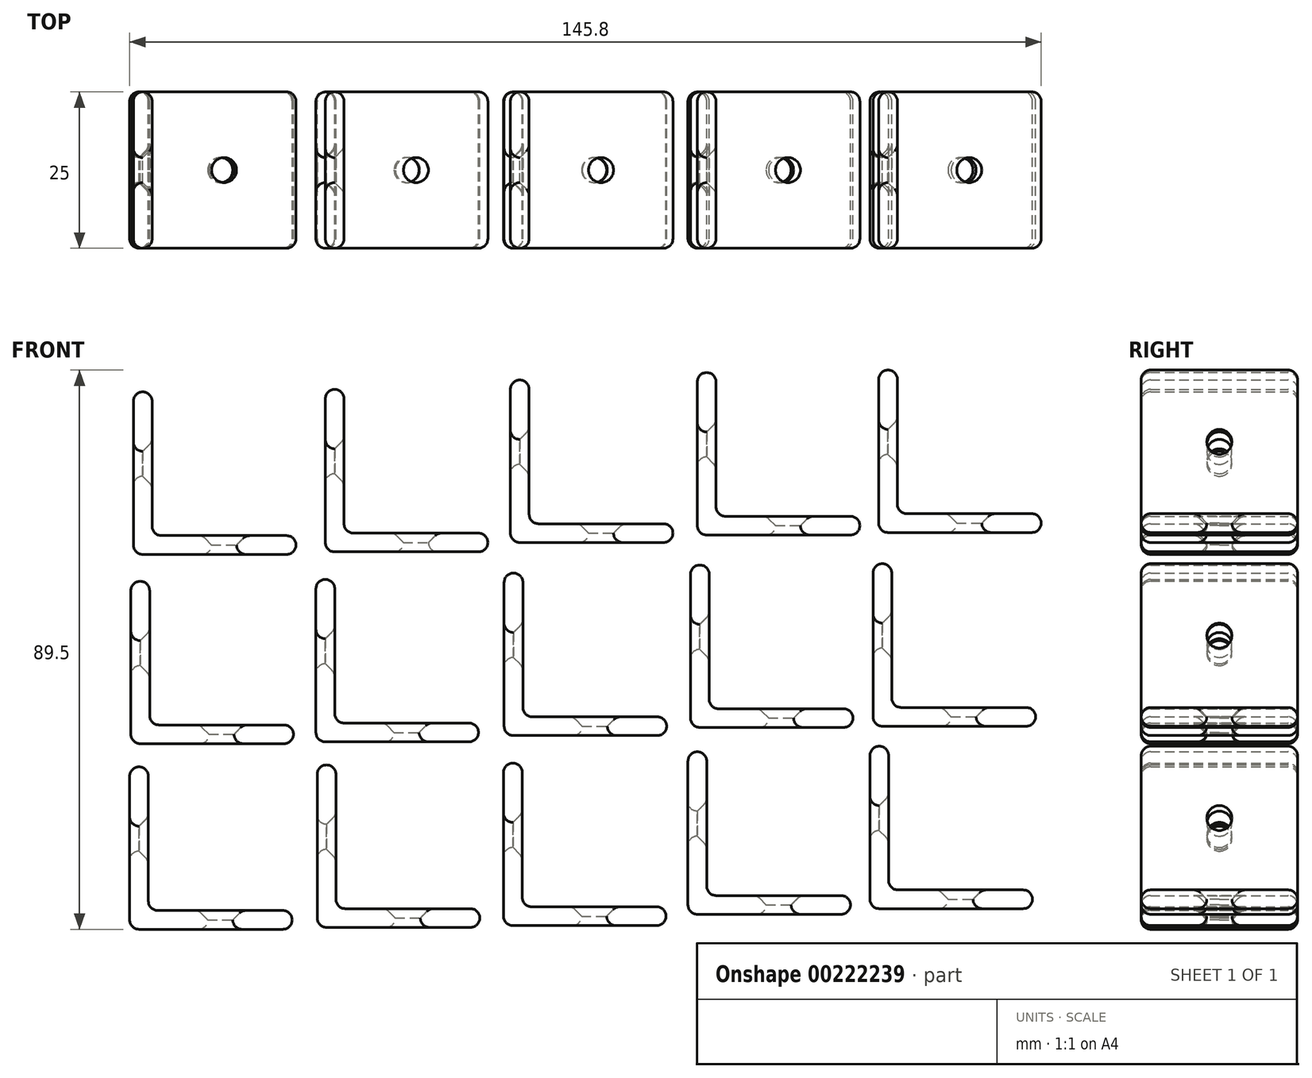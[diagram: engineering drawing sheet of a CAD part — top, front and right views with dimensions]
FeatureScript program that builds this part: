
annotation { "Feature Type Name" : "Feature", "Feature Type Description" : "" }
export const myFeature = defineFeature(function(context is Context, id is Id, definition is map)
    precondition{}
    {
        {
            var Q0;
            Q0=qCreatedBy(makeId("Front.planeOp"),FACE);
            var sketch = newSketch(context, id + "F0", { "sketchPlane" : qUnion([Q0])});
            skLineSegment(sketch, "E0.bottom", {"start": v(13, 13) * mm, "end": v(-13, 13) * mm});
            skLineSegment(sketch, "E0.top", {"start": v(13, -13) * mm, "end": v(-13, -13) * mm});
            skLineSegment(sketch, "E0.left", {"start": v(13, 13) * mm, "end": v(13, -13) * mm});
            skLineSegment(sketch, "E0.right", {"start": v(-13, 13) * mm, "end": v(-13, -13) * mm});
            skPoint(sketch, "E0.middle", {"position": v(0, 0) * mm});
            skLineSegment(sketch, "E1.bottom", {"start": v(13, 13) * mm, "end": v(-10, 13) * mm});
            skLineSegment(sketch, "E1.top", {"start": v(13, -10) * mm, "end": v(-10, -10) * mm});
            skLineSegment(sketch, "E1.left", {"start": v(13, 13) * mm, "end": v(13, -10) * mm});
            skLineSegment(sketch, "E1.right", {"start": v(-10, 13) * mm, "end": v(-10, -10) * mm});
            skSolve(sketch);
        }
        {
            var Q0;
            {var subQ2=sQuery(id+"F0.wireOp",EDGE,"E0.top");Q0=makeQuery(id+"F0.imprint","IMPRINT",FACE,{"disambiguationData":[TD([[makeQuery(id+"F0.imprint","IMPRINT",EDGE,{"derivedFrom":subQ2}),-1.0]])]});}
            extrude(context, id + "F1", {"entities" : qUnion([Q0]), "depth" : 25 * mm, "offsetDistance" : 25 * mm});
        }
        {
            var Q0;
            Q0=makeQuery(id+"F1.opExtrude","SWEPT_FACE",FACE,{"disambiguationData":[OSD([sQuery(id+"F0.wireOp",EDGE,"E1.right")])]});
            var sketch = newSketch(context, id + "F2", { "sketchPlane" : qUnion([Q0])});
            skLineSegment(sketch, "E2", {"start": v(-25, 13) * mm, "end": v(0, -10) * mm, "construction": true});
            skLineSegment(sketch, "E3", {"start": v(0, 13) * mm, "end": v(-25, -10) * mm, "construction": true});
            skPoint(sketch, "E4", {"position": v(-12.5, 1.5) * mm});
            skSolve(sketch);
        }
        {
            var Q0;
            Q0=makeQuery(id+"F1.opExtrude","SWEPT_FACE",FACE,{"disambiguationData":[OSD([sQuery(id+"F0.wireOp",EDGE,"E1.top")])]});
            var sketch = newSketch(context, id + "F3", { "sketchPlane" : qUnion([Q0])});
            skLineSegment(sketch, "E5", {"start": v(-10, -25) * mm, "end": v(13, 0) * mm, "construction": true});
            skLineSegment(sketch, "E6", {"start": v(-10, 0) * mm, "end": v(13, -25) * mm, "construction": true});
            skPoint(sketch, "E7", {"position": v(1.5, -12.5) * mm});
            skSolve(sketch);
        }
        {
            var Q0;
            Q0=sQuery(id+"F3.wireOp",VERTEX,"E7");
            var Q1;
            Q1=sQuery(id+"F2.wireOp",VERTEX,"E4");
            var Q2;
            Q2=makeQuery(id+"F1.opExtrude","SWEPT_BODY",BODY,{"disambiguationData":[OSD([sQuery(id+"F0.wireOp",EDGE,"E0.bottom"),sQuery(id+"F0.wireOp",EDGE,"E0.top"),sQuery(id+"F0.wireOp",EDGE,"E0.left"),sQuery(id+"F0.wireOp",EDGE,"E0.right"),sQuery(id+"F0.wireOp",EDGE,"E1.top"),sQuery(id+"F0.wireOp",EDGE,"E1.right")])]});
            hole(context, id + "F4", {"style" : HoleStyle.C_SINK, "endStyle" : HoleEndStyle.BLIND, "holeDiameter" : 4 * mm, "cSinkDiameter" : 7 * mm, "cSinkAngle" : 90 * degree, "majorDiameter" : 5 * mm, "holeDepth" : 7 * mm, "isTappedThrough" : true, "tappedDepth" : 12 * mm, "tapClearance" : 3, "locations" : qUnion([Q0, Q1]), "scope" : qUnion([Q2])});
        }
        {
            var Q0;
            Q0=makeQuery(id+"F1.opExtrude","SWEPT_FACE",FACE,{"disambiguationData":[OSD([sQuery(id+"F0.wireOp",EDGE,"E0.bottom")])]});
            var Q1;
            Q1=makeQuery(id+"F1.opExtrude","SWEPT_FACE",FACE,{"disambiguationData":[OSD([sQuery(id+"F0.wireOp",EDGE,"E0.right")])]});
            var Q2;
            Q2=makeQuery(id+"F1.opExtrude","SWEPT_FACE",FACE,{"disambiguationData":[OSD([sQuery(id+"F0.wireOp",EDGE,"E0.top")])]});
            var Q3;
            Q3=makeQuery(id+"F1.opExtrude","SWEPT_FACE",FACE,{"disambiguationData":[OSD([sQuery(id+"F0.wireOp",EDGE,"E0.left")])]});
            var Q4;
            Q4=makeQuery(id+"F1.opExtrude","SWEPT_FACE",FACE,{"disambiguationData":[OSD([sQuery(id+"F0.wireOp",EDGE,"E1.right")])]});
            var Q5;
            Q5=makeQuery(id+"F1.opExtrude","SWEPT_FACE",FACE,{"disambiguationData":[OSD([sQuery(id+"F0.wireOp",EDGE,"E1.top")])]});
            var Q6;
            Q6=makeQuery(id+"F1.opExtrude","CAP_FACE",FACE,{"disambiguationData":[OSD([sQuery(id+"F0.wireOp",EDGE,"E0.bottom"),sQuery(id+"F0.wireOp",EDGE,"E0.top"),sQuery(id+"F0.wireOp",EDGE,"E0.left"),sQuery(id+"F0.wireOp",EDGE,"E0.right"),sQuery(id+"F0.wireOp",EDGE,"E1.top"),sQuery(id+"F0.wireOp",EDGE,"E1.right")])],"isStart":true});
            var Q7;
            Q7=makeQuery(id+"F1.opExtrude","CAP_FACE",FACE,{"disambiguationData":[OSD([sQuery(id+"F0.wireOp",EDGE,"E0.bottom"),sQuery(id+"F0.wireOp",EDGE,"E0.top"),sQuery(id+"F0.wireOp",EDGE,"E0.left"),sQuery(id+"F0.wireOp",EDGE,"E0.right"),sQuery(id+"F0.wireOp",EDGE,"E1.top"),sQuery(id+"F0.wireOp",EDGE,"E1.right")])],"isStart":false});
            fillet(context, id + "F5", {"entities" : qUnion([Q0, Q1, Q2, Q3, Q4, Q5, Q6, Q7]), "radius" : 1.5 * mm, "tangentPropagation" : true, "allowEdgeOverflow" : false});
        }
        {
            var Q0;
            Q0=makeQuery(id+"F1.opExtrude","SWEPT_BODY",BODY,{"disambiguationData":[OSD([sQuery(id+"F0.wireOp",EDGE,"E0.bottom"),sQuery(id+"F0.wireOp",EDGE,"E0.top"),sQuery(id+"F0.wireOp",EDGE,"E0.left"),sQuery(id+"F0.wireOp",EDGE,"E0.right"),sQuery(id+"F0.wireOp",EDGE,"E1.top"),sQuery(id+"F0.wireOp",EDGE,"E1.right")])]});
            transform(context, id + "F6", {"entities" : qUnion([Q0]), "transformType" : TransformType.TRANSLATION_3D, "dx" : 29.8 * mm, "dy" : 0 * mm, "dz" : 1.3 * mm, "makeCopy" : true});
        }
        {
            var Q0;
            Q0=makeQuery(id+"F1.opExtrude","SWEPT_BODY",BODY,{"disambiguationData":[OSD([sQuery(id+"F0.wireOp",EDGE,"E0.bottom"),sQuery(id+"F0.wireOp",EDGE,"E0.top"),sQuery(id+"F0.wireOp",EDGE,"E0.left"),sQuery(id+"F0.wireOp",EDGE,"E0.right"),sQuery(id+"F0.wireOp",EDGE,"E1.top"),sQuery(id+"F0.wireOp",EDGE,"E1.right")])]});
            transform(context, id + "F7", {"entities" : qUnion([Q0]), "transformType" : TransformType.TRANSLATION_3D, "dx" : -30.1 * mm, "dy" : 0 * mm, "dz" : -1 * mm, "makeCopy" : true});
        }
        {
            var Q0;
            Q0=makeQuery(id+"F1.opExtrude","SWEPT_BODY",BODY,{"disambiguationData":[OSD([sQuery(id+"F0.wireOp",EDGE,"E0.bottom"),sQuery(id+"F0.wireOp",EDGE,"E0.top"),sQuery(id+"F0.wireOp",EDGE,"E0.left"),sQuery(id+"F0.wireOp",EDGE,"E0.right"),sQuery(id+"F0.wireOp",EDGE,"E1.top"),sQuery(id+"F0.wireOp",EDGE,"E1.right")])]});
            transform(context, id + "F8", {"entities" : qUnion([Q0]), "transformType" : TransformType.TRANSLATION_3D, "dx" : 1 * mm, "dy" : 0 * mm, "dz" : 30.9 * mm, "makeCopy" : true});
        }
        {
            var Q0;
            Q0=makeQuery(id+"F6.opPattern","COPY",BODY,{"derivedFrom":makeQuery(id+"F1.opExtrude","SWEPT_BODY",BODY,{"disambiguationData":[OSD([sQuery(id+"F0.wireOp",EDGE,"E0.bottom"),sQuery(id+"F0.wireOp",EDGE,"E0.top"),sQuery(id+"F0.wireOp",EDGE,"E0.left"),sQuery(id+"F0.wireOp",EDGE,"E0.right"),sQuery(id+"F0.wireOp",EDGE,"E1.top"),sQuery(id+"F0.wireOp",EDGE,"E1.right")])]}),"instanceName":"1"});
            transform(context, id + "F9", {"entities" : qUnion([Q0]), "transformType" : TransformType.TRANSLATION_3D, "dx" : 1.1 * mm, "dy" : 0 * mm, "dz" : 30.8 * mm, "makeCopy" : true});
        }
        {
            var Q0;
            Q0=makeQuery(id+"F7.opPattern","COPY",BODY,{"derivedFrom":makeQuery(id+"F1.opExtrude","SWEPT_BODY",BODY,{"disambiguationData":[OSD([sQuery(id+"F0.wireOp",EDGE,"E0.bottom"),sQuery(id+"F0.wireOp",EDGE,"E0.top"),sQuery(id+"F0.wireOp",EDGE,"E0.left"),sQuery(id+"F0.wireOp",EDGE,"E0.right"),sQuery(id+"F0.wireOp",EDGE,"E1.top"),sQuery(id+"F0.wireOp",EDGE,"E1.right")])]}),"instanceName":"1"});
            transform(context, id + "F10", {"entities" : qUnion([Q0]), "transformType" : TransformType.TRANSLATION_3D, "dx" : 1.5 * mm, "dy" : 0 * mm, "dz" : 30.4 * mm, "makeCopy" : true});
        }
        {
            var Q0;
            Q0=makeQuery(id+"F1.opExtrude","SWEPT_BODY",BODY,{"disambiguationData":[OSD([sQuery(id+"F0.wireOp",EDGE,"E0.bottom"),sQuery(id+"F0.wireOp",EDGE,"E0.top"),sQuery(id+"F0.wireOp",EDGE,"E0.left"),sQuery(id+"F0.wireOp",EDGE,"E0.right"),sQuery(id+"F0.wireOp",EDGE,"E1.top"),sQuery(id+"F0.wireOp",EDGE,"E1.right")])]});
            transform(context, id + "F11", {"entities" : qUnion([Q0]), "transformType" : TransformType.TRANSLATION_3D, "dx" : -0.1 * mm, "dy" : 0 * mm, "dz" : -30.4 * mm, "makeCopy" : true});
        }
        {
            var Q0;
            Q0=makeQuery(id+"F6.opPattern","COPY",BODY,{"derivedFrom":makeQuery(id+"F1.opExtrude","SWEPT_BODY",BODY,{"disambiguationData":[OSD([sQuery(id+"F0.wireOp",EDGE,"E0.bottom"),sQuery(id+"F0.wireOp",EDGE,"E0.top"),sQuery(id+"F0.wireOp",EDGE,"E0.left"),sQuery(id+"F0.wireOp",EDGE,"E0.right"),sQuery(id+"F0.wireOp",EDGE,"E1.top"),sQuery(id+"F0.wireOp",EDGE,"E1.right")])]}),"instanceName":"1"});
            transform(context, id + "F12", {"entities" : qUnion([Q0]), "transformType" : TransformType.TRANSLATION_3D, "dx" : -0.4 * mm, "dy" : 0 * mm, "dz" : -29.9 * mm, "makeCopy" : true});
        }
        {
            var Q0;
            Q0=makeQuery(id+"F7.opPattern","COPY",BODY,{"derivedFrom":makeQuery(id+"F1.opExtrude","SWEPT_BODY",BODY,{"disambiguationData":[OSD([sQuery(id+"F0.wireOp",EDGE,"E0.bottom"),sQuery(id+"F0.wireOp",EDGE,"E0.top"),sQuery(id+"F0.wireOp",EDGE,"E0.left"),sQuery(id+"F0.wireOp",EDGE,"E0.right"),sQuery(id+"F0.wireOp",EDGE,"E1.top"),sQuery(id+"F0.wireOp",EDGE,"E1.right")])]}),"instanceName":"1"});
            transform(context, id + "F13", {"entities" : qUnion([Q0]), "transformType" : TransformType.TRANSLATION_3D, "dx" : 0.2 * mm, "dy" : 0 * mm, "dz" : -29.7 * mm, "makeCopy" : true});
        }
        {
            var Q0;
            Q0=makeQuery(id+"F13.opPattern","COPY",BODY,{"derivedFrom":makeQuery(id+"F7.opPattern","COPY",BODY,{"derivedFrom":makeQuery(id+"F1.opExtrude","SWEPT_BODY",BODY,{"disambiguationData":[OSD([sQuery(id+"F0.wireOp",EDGE,"E0.bottom"),sQuery(id+"F0.wireOp",EDGE,"E0.top"),sQuery(id+"F0.wireOp",EDGE,"E0.left"),sQuery(id+"F0.wireOp",EDGE,"E0.right"),sQuery(id+"F0.wireOp",EDGE,"E1.top"),sQuery(id+"F0.wireOp",EDGE,"E1.right")])]}),"instanceName":"1"}),"instanceName":"1"});
            transform(context, id + "F14", {"entities" : qUnion([Q0]), "transformType" : TransformType.TRANSLATION_3D, "dx" : -30 * mm, "dy" : 0 * mm, "dz" : -0.3 * mm, "makeCopy" : true});
        }
        {
            var Q0;
            Q0=makeQuery(id+"F12.opPattern","COPY",BODY,{"derivedFrom":makeQuery(id+"F6.opPattern","COPY",BODY,{"derivedFrom":makeQuery(id+"F1.opExtrude","SWEPT_BODY",BODY,{"disambiguationData":[OSD([sQuery(id+"F0.wireOp",EDGE,"E0.bottom"),sQuery(id+"F0.wireOp",EDGE,"E0.top"),sQuery(id+"F0.wireOp",EDGE,"E0.left"),sQuery(id+"F0.wireOp",EDGE,"E0.right"),sQuery(id+"F0.wireOp",EDGE,"E1.top"),sQuery(id+"F0.wireOp",EDGE,"E1.right")])]}),"instanceName":"1"}),"instanceName":"1"});
            transform(context, id + "F15", {"entities" : qUnion([Q0]), "transformType" : TransformType.TRANSLATION_3D, "dx" : 29.1 * mm, "dy" : 0 * mm, "dz" : 0.9 * mm, "makeCopy" : true});
        }
        {
            var Q0;
            Q0=makeQuery(id+"F10.opPattern","COPY",BODY,{"derivedFrom":makeQuery(id+"F7.opPattern","COPY",BODY,{"derivedFrom":makeQuery(id+"F1.opExtrude","SWEPT_BODY",BODY,{"disambiguationData":[OSD([sQuery(id+"F0.wireOp",EDGE,"E0.bottom"),sQuery(id+"F0.wireOp",EDGE,"E0.top"),sQuery(id+"F0.wireOp",EDGE,"E0.left"),sQuery(id+"F0.wireOp",EDGE,"E0.right"),sQuery(id+"F0.wireOp",EDGE,"E1.top"),sQuery(id+"F0.wireOp",EDGE,"E1.right")])]}),"instanceName":"1"}),"instanceName":"1"});
            transform(context, id + "F16", {"entities" : qUnion([Q0]), "transformType" : TransformType.TRANSLATION_3D, "dx" : -30.7 * mm, "dy" : 0 * mm, "dz" : -0.4 * mm, "makeCopy" : true});
        }
        {
            var Q0;
            Q0=makeQuery(id+"F7.opPattern","COPY",BODY,{"derivedFrom":makeQuery(id+"F1.opExtrude","SWEPT_BODY",BODY,{"disambiguationData":[OSD([sQuery(id+"F0.wireOp",EDGE,"E0.bottom"),sQuery(id+"F0.wireOp",EDGE,"E0.top"),sQuery(id+"F0.wireOp",EDGE,"E0.left"),sQuery(id+"F0.wireOp",EDGE,"E0.right"),sQuery(id+"F0.wireOp",EDGE,"E1.top"),sQuery(id+"F0.wireOp",EDGE,"E1.right")])]}),"instanceName":"1"});
            transform(context, id + "F17", {"entities" : qUnion([Q0]), "transformType" : TransformType.TRANSLATION_3D, "dx" : -29.6 * mm, "dy" : 0 * mm, "dz" : -0.3 * mm, "makeCopy" : true});
        }
        {
            var Q0;
            Q0=makeQuery(id+"F6.opPattern","COPY",BODY,{"derivedFrom":makeQuery(id+"F1.opExtrude","SWEPT_BODY",BODY,{"disambiguationData":[OSD([sQuery(id+"F0.wireOp",EDGE,"E0.bottom"),sQuery(id+"F0.wireOp",EDGE,"E0.top"),sQuery(id+"F0.wireOp",EDGE,"E0.left"),sQuery(id+"F0.wireOp",EDGE,"E0.right"),sQuery(id+"F0.wireOp",EDGE,"E1.top"),sQuery(id+"F0.wireOp",EDGE,"E1.right")])]}),"instanceName":"1"});
            transform(context, id + "F18", {"entities" : qUnion([Q0]), "transformType" : TransformType.TRANSLATION_3D, "dx" : 29.2 * mm, "dy" : 0 * mm, "dz" : 0.2 * mm, "makeCopy" : true});
        }
        {
            var Q0;
            Q0=makeQuery(id+"F9.opPattern","COPY",BODY,{"derivedFrom":makeQuery(id+"F6.opPattern","COPY",BODY,{"derivedFrom":makeQuery(id+"F1.opExtrude","SWEPT_BODY",BODY,{"disambiguationData":[OSD([sQuery(id+"F0.wireOp",EDGE,"E0.bottom"),sQuery(id+"F0.wireOp",EDGE,"E0.top"),sQuery(id+"F0.wireOp",EDGE,"E0.left"),sQuery(id+"F0.wireOp",EDGE,"E0.right"),sQuery(id+"F0.wireOp",EDGE,"E1.top"),sQuery(id+"F0.wireOp",EDGE,"E1.right")])]}),"instanceName":"1"}),"instanceName":"1"});
            transform(context, id + "F19", {"entities" : qUnion([Q0]), "transformType" : TransformType.TRANSLATION_3D, "dx" : 29 * mm, "dy" : 0 * mm, "dz" : 0.4 * mm, "makeCopy" : true});
        }
    });
